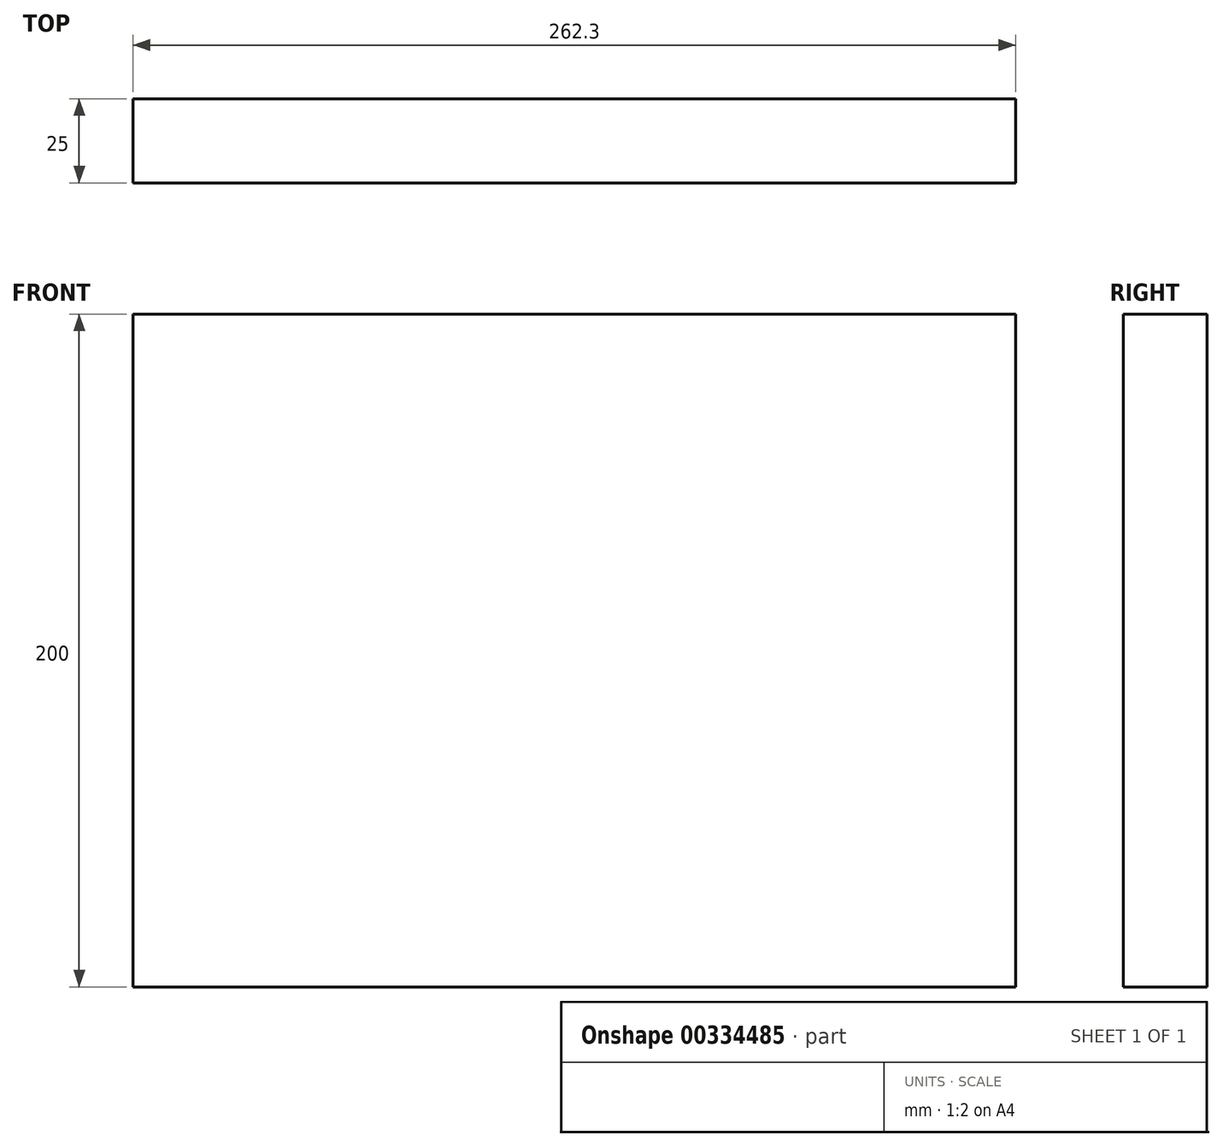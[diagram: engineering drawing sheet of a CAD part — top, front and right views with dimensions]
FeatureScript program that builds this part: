
annotation { "Feature Type Name" : "Feature", "Feature Type Description" : "" }
export const myFeature = defineFeature(function(context is Context, id is Id, definition is map)
    precondition{}
    {
        {
            var Q0;
            Q0=qCreatedBy(makeId("Front.planeOp"),FACE);
            var sketch = newSketch(context, id + "F0", { "sketchPlane" : qUnion([Q0])});
            skLineSegment(sketch, "E0.bottom", {"start": v(0, 0) * mm, "end": v(262.3, 0) * mm});
            skLineSegment(sketch, "E0.top", {"start": v(0, 200) * mm, "end": v(262.3, 200) * mm});
            skLineSegment(sketch, "E0.left", {"start": v(0, 0) * mm, "end": v(0, 200) * mm});
            skLineSegment(sketch, "E0.right", {"start": v(262.3, 0) * mm, "end": v(262.3, 200) * mm});
            skSolve(sketch);
        }
        {
            var Q0;
            Q0 = qSketchRegion(id + "F0", true);
            extrude(context, id + "F1", {"entities" : qUnion([Q0]), "depth" : 25 * mm});
        }
    });
